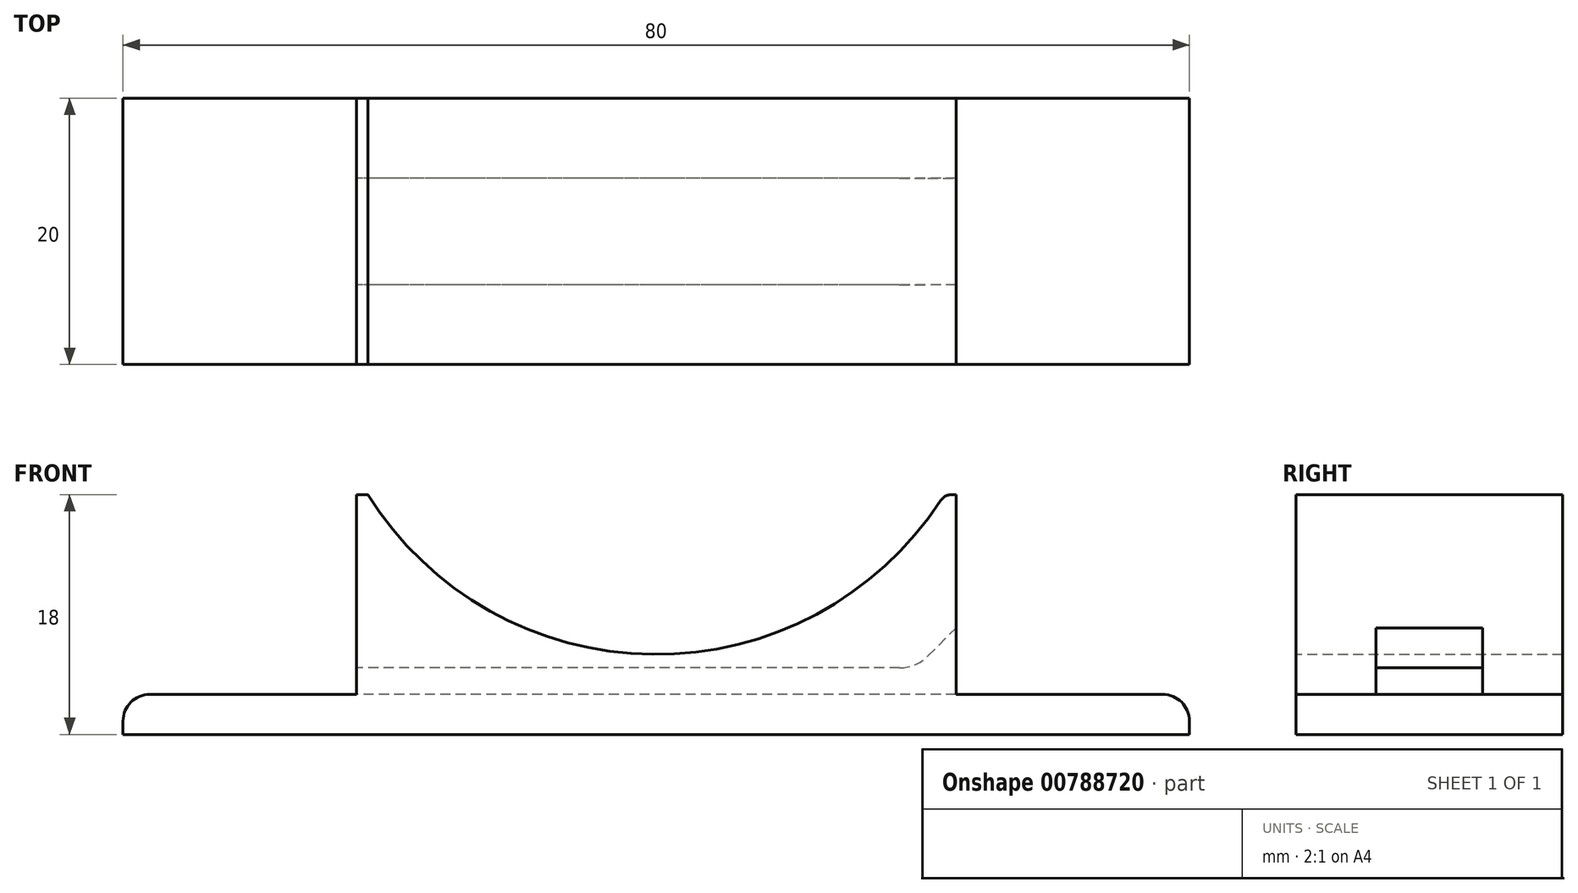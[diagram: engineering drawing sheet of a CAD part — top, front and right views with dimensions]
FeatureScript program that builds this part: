
annotation { "Feature Type Name" : "Feature", "Feature Type Description" : "" }
export const myFeature = defineFeature(function(context is Context, id is Id, definition is map)
    precondition{}
    {
        {
            var Q0;
            Q0=qCreatedBy(makeId("Top.planeOp"),FACE);
            var sketch = newSketch(context, id + "F0", { "sketchPlane" : qUnion([Q0])});
            skLineSegment(sketch, "E0.bottom", {"start": v(-40, 10) * mm, "end": v(40, 10) * mm});
            skLineSegment(sketch, "E0.top", {"start": v(-40, -10) * mm, "end": v(40, -10) * mm});
            skLineSegment(sketch, "E0.left", {"start": v(-40, 10) * mm, "end": v(-40, -10) * mm});
            skLineSegment(sketch, "E0.right", {"start": v(40, 10) * mm, "end": v(40, -10) * mm});
            skPoint(sketch, "E0.middle", {"position": v(0, 0) * mm});
            skSolve(sketch);
        }
        {
            var Q0;
            Q0=makeQuery(id+"F0.imprint","IMPRINT",FACE,{"disambiguationData":[TD([[makeQuery(id+"F0.imprint","IMPRINT",EDGE,{"derivedFrom":sQuery(id+"F0.wireOp",EDGE,"E0.bottom")}),-1.0]])]});
            extrude(context, id + "F1", {"entities" : qUnion([Q0]), "endBound" : BoundingType.SYMMETRIC, "oppositeDirection" : true, "depth" : 3 * mm, "offsetDistance" : 25 * mm});
        }
        {
            var Q0;
            Q0=makeQuery(id+"F1.opExtrude","CAP_FACE",FACE,{"disambiguationData":[OSD([sQuery(id+"F0.wireOp",EDGE,"E0.bottom"),sQuery(id+"F0.wireOp",EDGE,"E0.top"),sQuery(id+"F0.wireOp",EDGE,"E0.left"),sQuery(id+"F0.wireOp",EDGE,"E0.right")])],"isStart":true});
            var sketch = newSketch(context, id + "F2", { "sketchPlane" : qUnion([Q0])});
            skLineSegment(sketch, "E1.bottom", {"start": v(-22.5, 10) * mm, "end": v(22.5, 10) * mm});
            skLineSegment(sketch, "E1.top", {"start": v(-22.5, -10) * mm, "end": v(22.5, -10) * mm});
            skLineSegment(sketch, "E1.left", {"start": v(-22.5, 10) * mm, "end": v(-22.5, -10) * mm});
            skLineSegment(sketch, "E1.right", {"start": v(22.5, 10) * mm, "end": v(22.5, -10) * mm});
            skPoint(sketch, "E1.middle", {"position": v(0, 0) * mm});
            skSolve(sketch);
        }
        {
            var Q0;
            Q0 = qSketchRegion(id + "F2", true);
            extrude(context, id + "F3", {"entities" : qUnion([Q0]), "operationType" : NewBodyOperationType.ADD, "depth" : 15 * mm, "offsetDistance" : 25 * mm});
        }
        {
            var Q0;
            Q0=makeQuery(id+"F3.opExtrude","SWEPT_FACE",FACE,{"disambiguationData":[OSD([sQuery(id+"F2.wireOp",EDGE,"E1.left")])]});
            var sketch = newSketch(context, id + "F4", { "sketchPlane" : qUnion([Q0])});
            skLineSegment(sketch, "E2.bottom", {"start": v(-4, 1.5) * mm, "end": v(4, 1.5) * mm});
            skLineSegment(sketch, "E2.top", {"start": v(-4, 3.5) * mm, "end": v(4, 3.5) * mm});
            skLineSegment(sketch, "E2.left", {"start": v(-4, 1.5) * mm, "end": v(-4, 3.5) * mm});
            skLineSegment(sketch, "E2.right", {"start": v(4, 1.5) * mm, "end": v(4, 3.5) * mm});
            skSolve(sketch);
        }
        {
            var Q0;
            Q0=makeQuery(id+"F4.imprint","IMPRINT",FACE,{"disambiguationData":[TD([[makeQuery(id+"F4.imprint","IMPRINT",EDGE,{"derivedFrom":sQuery(id+"F4.wireOp",EDGE,"E2.bottom")}),1.0]])]});
            extrude(context, id + "F5", {"entities" : qUnion([Q0]), "operationType" : NewBodyOperationType.REMOVE, "oppositeDirection" : true, "depth" : 55 * mm, "offsetDistance" : 25 * mm});
        }
        {
            var Q0;
            Q0=makeQuery(id+"F1.opExtrude","CAP_EDGE",EDGE,{"disambiguationData":[OSD([sQuery(id+"F0.wireOp",EDGE,"E0.left")])],"isStart":true});
            var Q1;
            Q1=makeQuery(id+"F1.opExtrude","CAP_EDGE",EDGE,{"disambiguationData":[OSD([sQuery(id+"F0.wireOp",EDGE,"E0.right")])],"isStart":true});
            fillet(context, id + "F6", {"entities" : qUnion([Q0, Q1]), "radius" : 2 * mm, "tangentPropagation" : true, "allowEdgeOverflow" : false});
        }
        {
            var Q0;
            Q0=makeQuery(id+"F3.boolean.opBoolean","MERGE",FACE,{"derivedFrom":[makeQuery(id+"F1.opExtrude","SWEPT_FACE",FACE,{"disambiguationData":[OSD([sQuery(id+"F0.wireOp",EDGE,"E0.top")])]}),makeQuery(id+"F3.opExtrude","SWEPT_FACE",FACE,{"disambiguationData":[OSD([sQuery(id+"F2.wireOp",EDGE,"E1.top")])]})]});
            var sketch = newSketch(context, id + "F7", { "sketchPlane" : qUnion([Q0])});
            skLineSegment(sketch, "E3", {"start": v(0, -8.34) * mm, "end": v(0, 53.8) * mm, "construction": true});
            skCircle(sketch, "E4", {"center": v(0, 30) * mm, "radius": 25.5 * mm});
            skSolve(sketch);
        }
        {
            var Q0;
            {var subQ1=sQuery(id+"F2.wireOp",EDGE,"E1.top");var subQ7=makeQuery(id+"F3.opExtrude","CAP_EDGE",EDGE,{"disambiguationData":[OSD([subQ1])],"isStart":false});Q0=makeQuery(id+"F7.imprint","IMPRINT",FACE,{"disambiguationData":[TD([[makeQuery(id+"F7.imprint","IMPRINT",EDGE,{"derivedFrom":subQ7}),-1.0]])]});}
            extrude(context, id + "F8", {"entities" : qUnion([Q0]), "operationType" : NewBodyOperationType.REMOVE, "oppositeDirection" : true, "depth" : 20 * mm, "offsetDistance" : 25 * mm});
        }
        {
            var Q0;
            {var subQ0=sQuery(id+"F7.wireOp",EDGE,"E4");var subQ1=sQuery(id+"F2.wireOp",EDGE,"E1.top");Q0=makeQuery(id+"F8.boolean.opBoolean","COPY",EDGE,{"derivedFrom":makeQuery(id+"F8.opExtrude","SWEPT_EDGE",EDGE,{"disambiguationData":[OSD([subQ1,subQ0]),TDD([makeQuery(id+"F7.imprint","INTERSECT",VERTEX,{"disambiguationData":[OD(1.0)],"derivedFrom":[makeQuery(id+"F3.opExtrude","CAP_EDGE",EDGE,{"disambiguationData":[OSD([subQ1])],"isStart":false}),subQ0]})])]})});}
            var Q1;
            {var subQ0=sQuery(id+"F7.wireOp",EDGE,"E4");var subQ1=sQuery(id+"F2.wireOp",EDGE,"E1.top");Q1=makeQuery(id+"F8.boolean.opBoolean","COPY",EDGE,{"derivedFrom":makeQuery(id+"F8.opExtrude","SWEPT_EDGE",EDGE,{"disambiguationData":[OSD([subQ1,subQ0]),TDD([makeQuery(id+"F7.imprint","INTERSECT",VERTEX,{"disambiguationData":[OD(0.0)],"derivedFrom":[makeQuery(id+"F3.opExtrude","CAP_EDGE",EDGE,{"disambiguationData":[OSD([subQ1])],"isStart":false}),subQ0]})])]})});}
            fillet(context, id + "F9", {"entities" : qUnion([Q0, Q1]), "radius" : 1 * mm, "tangentPropagation" : true, "allowEdgeOverflow" : false});
        }
        {
            var Q0;
            Q0=makeQuery(id+"F5.boolean.opBoolean","INTERSECT",EDGE,{"derivedFrom":[makeQuery(id+"F3.opExtrude","SWEPT_FACE",FACE,{"disambiguationData":[OSD([sQuery(id+"F2.wireOp",EDGE,"E1.right")])]}),makeQuery(id+"F5.opExtrude","SWEPT_FACE",FACE,{"disambiguationData":[OSD([sQuery(id+"F4.wireOp",EDGE,"E2.top")])]})]});
            var Q1;
            Q1=makeQuery(id+"F5.boolean.opBoolean","COPY",EDGE,{"derivedFrom":makeQuery(id+"F5.opExtrude","CAP_EDGE",EDGE,{"disambiguationData":[OSD([sQuery(id+"F4.wireOp",EDGE,"E2.top")])],"isStart":true})});
            chamfer(context, id + "F10", {"entities" : qUnion([Q0, Q1]), "width" : 3 * mm, "tangentPropagation" : true});
        }
        {
            var Q0;
            {var subQ0=sQuery(id+"F4.wireOp",EDGE,"E2.top");Q0=makeQuery(id+"F10.opChamfer","BLEND_EDGE",EDGE,{"blendedFrom":[makeQuery(id+"F5.boolean.opBoolean","COPY",EDGE,{"derivedFrom":makeQuery(id+"F5.opExtrude","CAP_EDGE",EDGE,{"disambiguationData":[OSD([subQ0])],"isStart":true})}),makeQuery(id+"F5.boolean.opBoolean","COPY",FACE,{"derivedFrom":makeQuery(id+"F5.opExtrude","SWEPT_FACE",FACE,{"disambiguationData":[OSD([subQ0])]})})],"blendedInto":[makeQuery(id+"F5.boolean.opBoolean","COPY",FACE,{"derivedFrom":makeQuery(id+"F5.opExtrude","SWEPT_FACE",FACE,{"disambiguationData":[OSD([subQ0])]})})]});}
            var Q1;
            {var subQ0=makeQuery(id+"F5.opExtrude","SWEPT_FACE",FACE,{"disambiguationData":[OSD([sQuery(id+"F4.wireOp",EDGE,"E2.top")])]});Q1=makeQuery(id+"F10.opChamfer","BLEND_EDGE",EDGE,{"blendedFrom":[makeQuery(id+"F5.boolean.opBoolean","INTERSECT",EDGE,{"derivedFrom":[makeQuery(id+"F3.opExtrude","SWEPT_FACE",FACE,{"disambiguationData":[OSD([sQuery(id+"F2.wireOp",EDGE,"E1.right")])]}),subQ0]}),makeQuery(id+"F5.boolean.opBoolean","COPY",FACE,{"derivedFrom":subQ0})],"blendedInto":[makeQuery(id+"F5.boolean.opBoolean","COPY",FACE,{"derivedFrom":subQ0})]});}
            fillet(context, id + "F11", {"entities" : qUnion([Q0, Q1]), "radius" : 3 * mm, "tangentPropagation" : true, "allowEdgeOverflow" : false});
        }
    });
